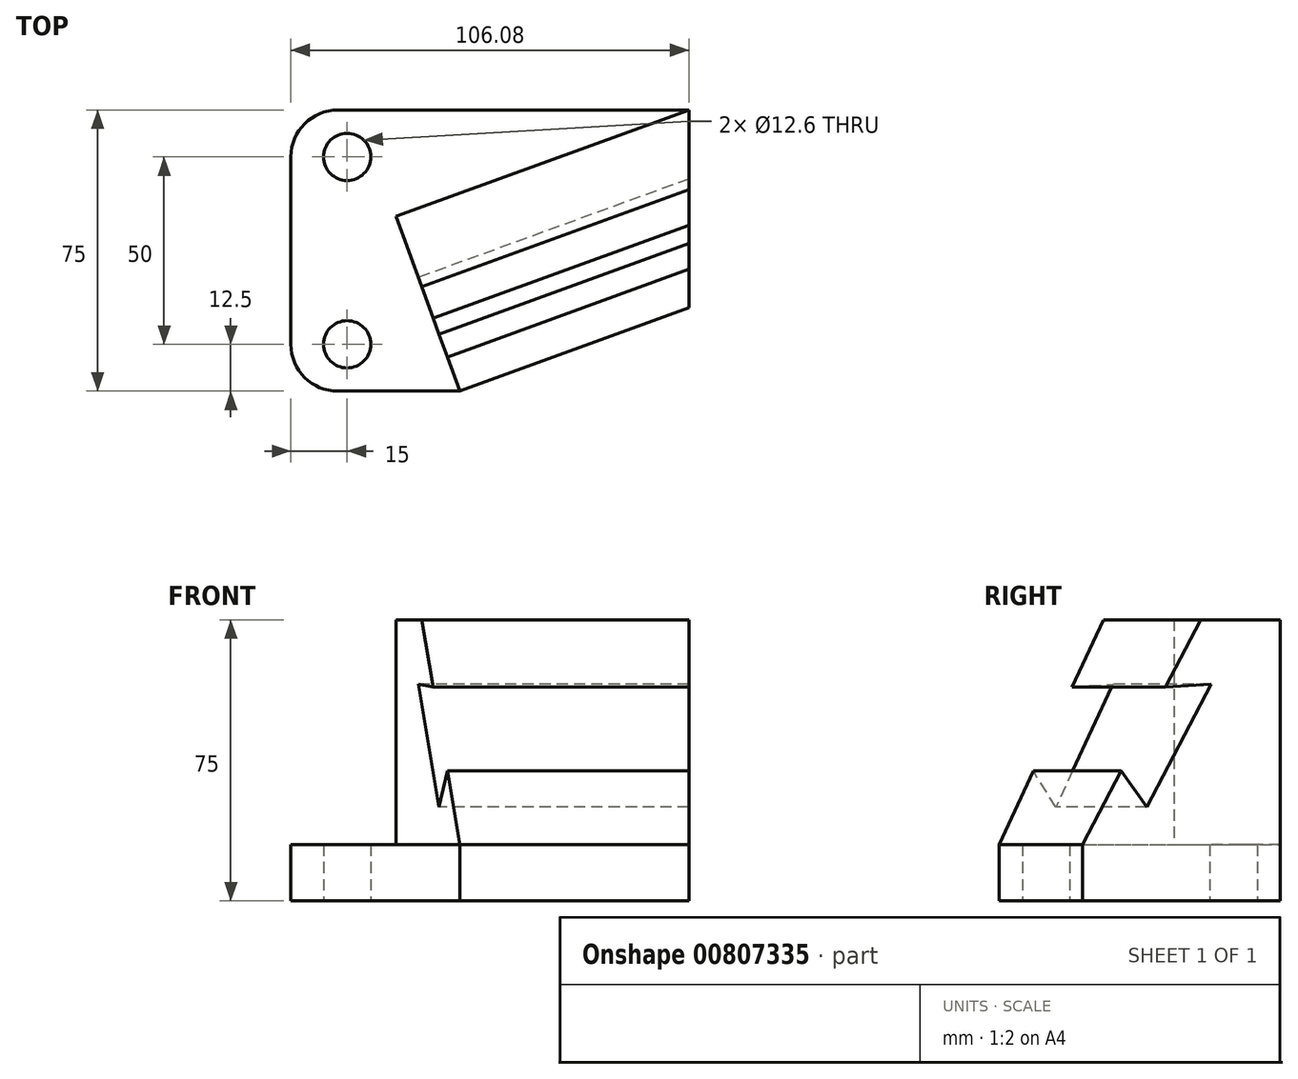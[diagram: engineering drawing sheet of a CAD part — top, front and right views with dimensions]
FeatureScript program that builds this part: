
annotation { "Feature Type Name" : "Feature", "Feature Type Description" : "" }
export const myFeature = defineFeature(function(context is Context, id is Id, definition is map)
    precondition{}
    {
        {
            var Q0;
            Q0=qCreatedBy(makeId("Top.planeOp"),FACE);
            var sketch = newSketch(context, id + "F0", { "sketchPlane" : qUnion([Q0])});
            skLineSegment(sketch, "E0", {"start": v(0, 12.5) * mm, "end": v(0, 62.5) * mm});
            skLineSegment(sketch, "E1", {"start": v(12.5, 0) * mm, "end": v(45, 0) * mm});
            skLineSegment(sketch, "E2", {"start": v(45, 0) * mm, "end": v(106.08, 22.23) * mm});
            skLineSegment(sketch, "E3", {"start": v(106.08, 22.23) * mm, "end": v(106.08, 75) * mm});
            skLineSegment(sketch, "E4", {"start": v(106.08, 75) * mm, "end": v(12.5, 75) * mm});
            skLineSegment(sketch, "E5", {"start": v(45, 0) * mm, "end": v(28.04, 46.6) * mm});
            skLineSegment(sketch, "E6", {"start": v(28.04, 46.6) * mm, "end": v(106.08, 75) * mm});
            skLineSegment(sketch, "E7", {"start": v(15, 75) * mm, "end": v(15, 0) * mm, "construction": true});
            skPoint(sketch, "E8", {"position": v(15, 37.5) * mm});
            skCircle(sketch, "E9", {"center": v(15, 62.5) * mm, "radius": 6.3 * mm});
            skCircle(sketch, "E10", {"center": v(15, 12.5) * mm, "radius": 6.3 * mm});
            skPoint(sketch, "E11.visualSharp", {"position": v(0, 75) * mm});
            skArc(sketch, "E11.filletArc", {"start": v(12.5, 75) * mm, "mid": v(3.66, 71.34) * mm, "end": v(0, 62.5) * mm});
            skPoint(sketch, "E12.visualSharp", {"position": v(0, 0) * mm});
            skArc(sketch, "E12.filletArc", {"start": v(0, 12.5) * mm, "mid": v(3.66, 3.66) * mm, "end": v(12.5, 0) * mm});
            skSolve(sketch);
        }
        {
            var Q0;
            Q0=makeQuery(id+"F0.imprint","IMPRINT",FACE,{"disambiguationData":[TD([[makeQuery(id+"F0.imprint","IMPRINT",EDGE,{"derivedFrom":sQuery(id+"F0.wireOp",EDGE,"E0")}),-1.0]])]});
            extrude(context, id + "F1", {"entities" : qUnion([Q0]), "depth" : 15 * mm, "offsetDistance" : 25 * mm});
        }
        {
            var Q0;
            Q0=makeQuery(id+"F0.imprint","IMPRINT",FACE,{"disambiguationData":[TD([[makeQuery(id+"F0.imprint","IMPRINT",EDGE,{"derivedFrom":sQuery(id+"F0.wireOp",EDGE,"E2")}),1.0]])]});
            extrude(context, id + "F2", {"entities" : qUnion([Q0]), "operationType" : NewBodyOperationType.ADD, "depth" : 75 * mm, "offsetDistance" : 25 * mm});
        }
        {
            var Q0;
            Q0=makeQuery(id+"F2.opExtrude","SWEPT_FACE",FACE,{"disambiguationData":[OSD([sQuery(id+"F0.wireOp",EDGE,"E5")])]});
            var sketch = newSketch(context, id + "F3", { "sketchPlane" : qUnion([Q0])});
            skLineSegment(sketch, "E13.0.0", {"start": v(-34.2, 15) * mm, "end": v(15.4, 15) * mm});
            skLineSegment(sketch, "E13.0.1", {"start": v(15.4, 15) * mm, "end": v(15.4, 75) * mm});
            skLineSegment(sketch, "E13.0.2", {"start": v(15.4, 75) * mm, "end": v(-34.2, 75) * mm});
            skLineSegment(sketch, "E13.0.3", {"start": v(-34.2, 75) * mm, "end": v(-34.2, 15) * mm});
            skLineSegment(sketch, "E14", {"start": v(-14.2, 75) * mm, "end": v(15.4, 15) * mm});
            skLineSegment(sketch, "E15", {"start": v(-5.35, 57.06) * mm, "end": v(-16.87, 57.82) * mm});
            skLineSegment(sketch, "E16", {"start": v(-16.87, 57.82) * mm, "end": v(-0.7, 25.04) * mm});
            skLineSegment(sketch, "E17", {"start": v(-0.7, 25.04) * mm, "end": v(5.7, 34.64) * mm});
            skSolve(sketch);
        }
        {
            var Q0;
            {var subQ0=sQuery(id+"F3.wireOp",EDGE,"E15");Q0=makeQuery(id+"F3.imprint","IMPRINT",FACE,{"disambiguationData":[TD([[makeQuery(id+"F3.imprint","IMPRINT",EDGE,{"derivedFrom":subQ0}),1.0]])]});}
            var Q1;
            {var subQ4=sQuery(id+"F3.wireOp",EDGE,"E13.0.1");Q1=makeQuery(id+"F3.imprint","IMPRINT",FACE,{"disambiguationData":[TD([[makeQuery(id+"F3.imprint","IMPRINT",EDGE,{"derivedFrom":subQ4}),-1.0]])]});}
            extrude(context, id + "F4", {"entities" : qUnion([Q0, Q1]), "operationType" : NewBodyOperationType.REMOVE, "endBound" : BoundingType.THROUGH_ALL, "oppositeDirection" : true, "depth" : 25 * mm, "offsetDistance" : 25 * mm});
        }
    });
